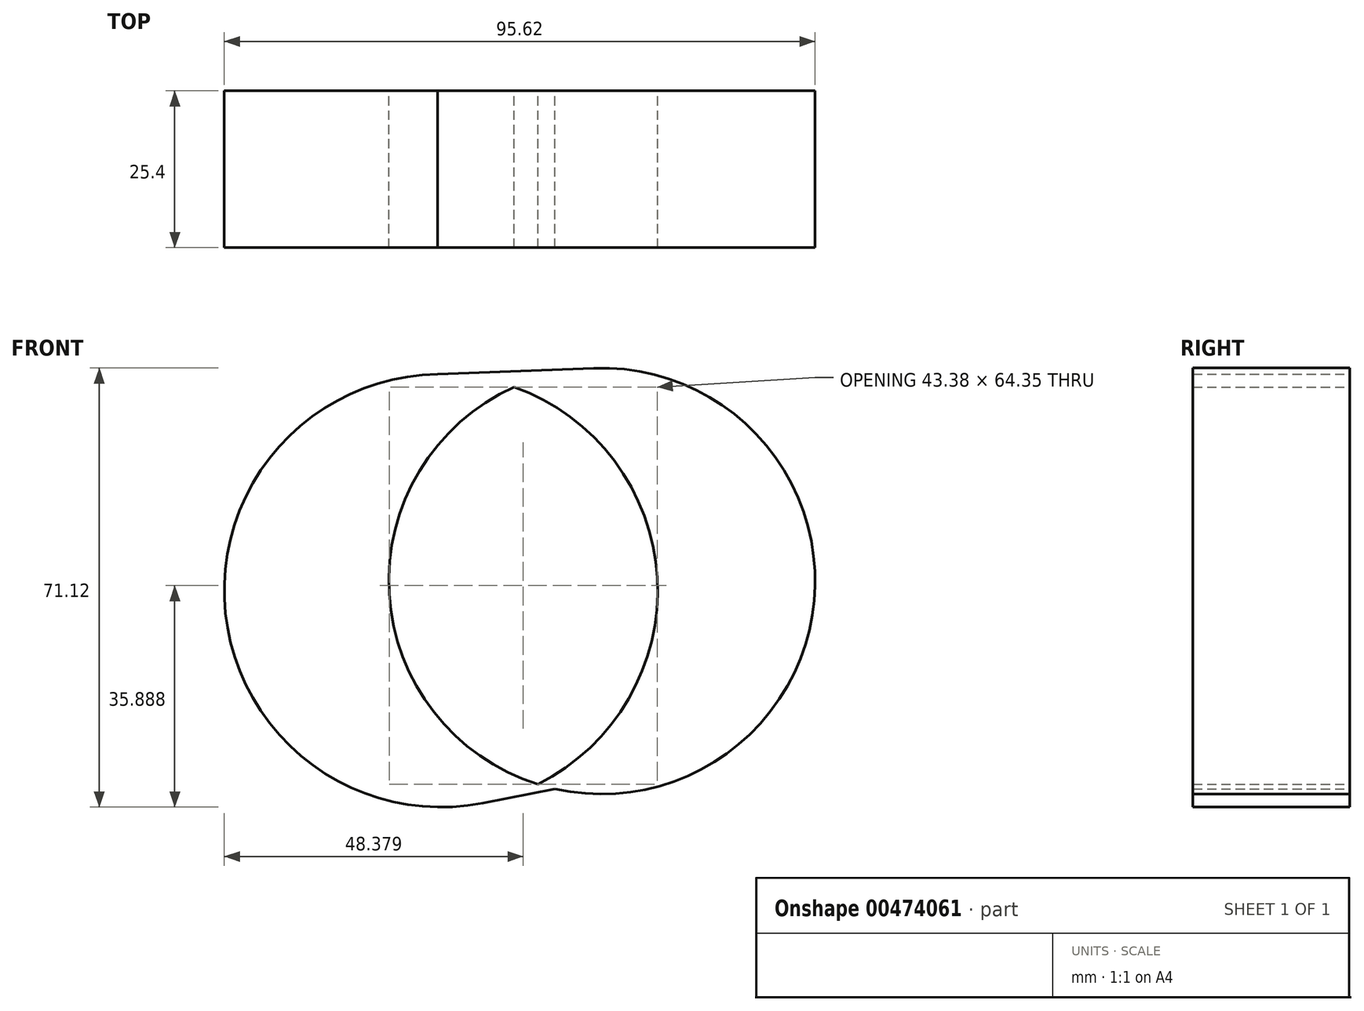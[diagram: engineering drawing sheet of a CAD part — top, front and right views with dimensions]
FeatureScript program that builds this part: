
annotation { "Feature Type Name" : "Feature", "Feature Type Description" : "" }
export const myFeature = defineFeature(function(context is Context, id is Id, definition is map)
    precondition{}
    {
        {
            var Q0;
            Q0=qCreatedBy(makeId("Front.planeOp"),FACE);
            var sketch = newSketch(context, id + "F0", { "sketchPlane" : qUnion([Q0])});
            skCircle(sketch, "E0", {"center": v(-54.48, 45.78) * mm, "radius": 34.5 * mm});
            skCircle(sketch, "E1", {"center": v(-80.53, 44.23) * mm, "radius": 35.07 * mm});
            skLineSegment(sketch, "E2", {"start": v(-82.68, 79.23) * mm, "end": v(-55.79, 80.25) * mm});
            skLineSegment(sketch, "E3", {"start": v(-73.74, 9.82) * mm, "end": v(-62.07, 12.13) * mm});
            skLineSegment(sketch, "E4", {"start": v(-80.53, 44.23) * mm, "end": v(-54.48, 45.78) * mm});
            skSolve(sketch);
        }
        {
            var Q0;
            Q0 = qSketchRegion(id + "F0", true);
            extrude(context, id + "F1", {"entities" : qUnion([Q0]), "depth" : 25.4 * mm});
        }
    });
